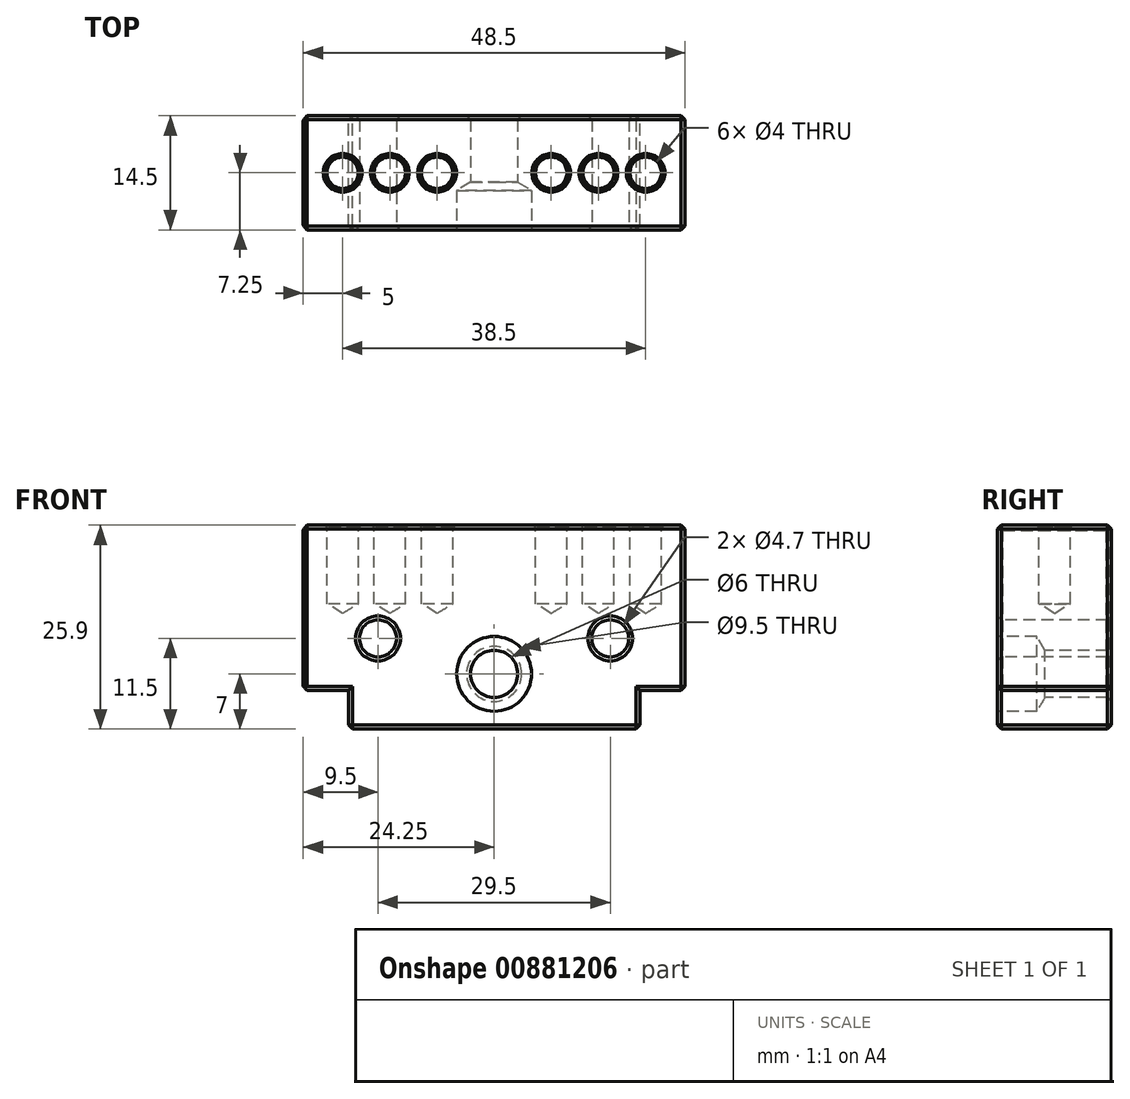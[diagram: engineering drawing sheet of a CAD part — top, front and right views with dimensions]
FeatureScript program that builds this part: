
annotation { "Feature Type Name" : "Feature", "Feature Type Description" : "" }
export const myFeature = defineFeature(function(context is Context, id is Id, definition is map)
    precondition{}
    {
        {
            var Q0;
            Q0=qCreatedBy(makeId("Front.planeOp"),FACE);
            var sketch = newSketch(context, id + "F0", { "sketchPlane" : qUnion([Q0])});
            skLineSegment(sketch, "E0", {"start": v(0, 4.9) * mm, "end": v(5.75, 4.9) * mm});
            skLineSegment(sketch, "E1", {"start": v(5.75, 4.9) * mm, "end": v(5.75, 0) * mm});
            skLineSegment(sketch, "E2", {"start": v(5.75, 0) * mm, "end": v(42.75, 0) * mm});
            skLineSegment(sketch, "E3", {"start": v(42.75, 0) * mm, "end": v(42.75, 4.9) * mm});
            skLineSegment(sketch, "E4", {"start": v(42.75, 4.9) * mm, "end": v(48.5, 4.9) * mm});
            skLineSegment(sketch, "E5", {"start": v(48.5, 4.9) * mm, "end": v(48.5, 25.9) * mm});
            skLineSegment(sketch, "E6", {"start": v(48.5, 25.9) * mm, "end": v(0, 25.9) * mm});
            skLineSegment(sketch, "E7", {"start": v(0, 25.9) * mm, "end": v(0, 4.9) * mm});
            skSolve(sketch);
        }
        {
            var Q0;
            Q0=makeQuery(id+"F0.imprint","IMPRINT",FACE,{"disambiguationData":[TD([[makeQuery(id+"F0.imprint","IMPRINT",EDGE,{"derivedFrom":sQuery(id+"F0.wireOp",EDGE,"E0")}),1.0]])]});
            extrude(context, id + "F1", {"entities" : qUnion([Q0]), "depth" : 14.5 * mm, "offsetDistance" : 25 * mm});
        }
        {
            var Q0;
            Q0=makeQuery(id+"F1.opExtrude","CAP_FACE",FACE,{"disambiguationData":[OSD([sQuery(id+"F0.wireOp",EDGE,"E0"),sQuery(id+"F0.wireOp",EDGE,"E1"),sQuery(id+"F0.wireOp",EDGE,"E2"),sQuery(id+"F0.wireOp",EDGE,"E3"),sQuery(id+"F0.wireOp",EDGE,"E4"),sQuery(id+"F0.wireOp",EDGE,"E5"),sQuery(id+"F0.wireOp",EDGE,"E6"),sQuery(id+"F0.wireOp",EDGE,"E7")])],"isStart":false});
            var sketch = newSketch(context, id + "F2", { "sketchPlane" : qUnion([Q0])});
            skPoint(sketch, "E8", {"position": v(24.25, 7) * mm});
            skPoint(sketch, "E9", {"position": v(9.5, 11.5) * mm});
            skPoint(sketch, "E10", {"position": v(39, 11.5) * mm});
            skPoint(sketch, "E11.end.orphan", {"position": v(0, 7) * mm});
            skSolve(sketch);
        }
        {
            var Q0;
            Q0=sQuery(id+"F2.wireOp",VERTEX,"E9");
            var Q1;
            Q1=sQuery(id+"F2.wireOp",VERTEX,"E10");
            var Q2;
            Q2=makeQuery(id+"F1.opExtrude","SWEPT_BODY",BODY,{"disambiguationData":[OSD([sQuery(id+"F0.wireOp",EDGE,"E0"),sQuery(id+"F0.wireOp",EDGE,"E1"),sQuery(id+"F0.wireOp",EDGE,"E2"),sQuery(id+"F0.wireOp",EDGE,"E3"),sQuery(id+"F0.wireOp",EDGE,"E4"),sQuery(id+"F0.wireOp",EDGE,"E5"),sQuery(id+"F0.wireOp",EDGE,"E6"),sQuery(id+"F0.wireOp",EDGE,"E7")])]});
            hole(context, id + "F3", {"style" : HoleStyle.SIMPLE, "endStyle" : HoleEndStyle.THROUGH, "holeDiameter" : 4.7 * mm, "majorDiameter" : 5 * mm, "isTappedThrough" : true, "tappedDepth" : 6 * mm, "tapClearance" : 3, "locations" : qUnion([Q0, Q1]), "scope" : qUnion([Q2])});
        }
        {
            var Q0;
            Q0=sQuery(id+"F2.wireOp",VERTEX,"E8");
            var Q1;
            Q1=makeQuery(id+"F1.opExtrude","SWEPT_BODY",BODY,{"disambiguationData":[OSD([sQuery(id+"F0.wireOp",EDGE,"E0"),sQuery(id+"F0.wireOp",EDGE,"E1"),sQuery(id+"F0.wireOp",EDGE,"E2"),sQuery(id+"F0.wireOp",EDGE,"E3"),sQuery(id+"F0.wireOp",EDGE,"E4"),sQuery(id+"F0.wireOp",EDGE,"E5"),sQuery(id+"F0.wireOp",EDGE,"E6"),sQuery(id+"F0.wireOp",EDGE,"E7")])]});
            hole(context, id + "F4", {"style" : HoleStyle.SIMPLE, "endStyle" : HoleEndStyle.THROUGH, "holeDiameter" : 6 * mm, "majorDiameter" : 5 * mm, "isTappedThrough" : true, "tappedDepth" : 6 * mm, "tapClearance" : 3, "locations" : qUnion([Q0]), "scope" : qUnion([Q1])});
        }
        {
            var Q0;
            Q0=makeQuery(id+"F1.opExtrude","SWEPT_FACE",FACE,{"disambiguationData":[OSD([sQuery(id+"F0.wireOp",EDGE,"E6")])]});
            var sketch = newSketch(context, id + "F5", { "sketchPlane" : qUnion([Q0])});
            skLineSegment(sketch, "E12", {"start": v(0, -7.25) * mm, "end": v(52.15, -7.25) * mm, "construction": true});
            skPoint(sketch, "E13", {"position": v(5, -7.25) * mm});
            skPoint(sketch, "E14", {"position": v(11, -7.25) * mm});
            skPoint(sketch, "E15", {"position": v(17, -7.25) * mm});
            skLineSegment(sketch, "E16", {"start": v(24.25, 0) * mm, "end": v(24.25, -16.26) * mm, "construction": true});
            skPoint(sketch, "E17.MirrorP", {"position": v(31.5, -7.25) * mm});
            skPoint(sketch, "E18.MirrorP", {"position": v(37.5, -7.25) * mm});
            skPoint(sketch, "E19.MirrorP", {"position": v(43.5, -7.25) * mm});
            skSolve(sketch);
        }
        {
            var Q0;
            Q0=sQuery(id+"F5.wireOp",VERTEX,"E13");
            var Q1;
            Q1=sQuery(id+"F5.wireOp",VERTEX,"E14");
            var Q2;
            Q2=sQuery(id+"F5.wireOp",VERTEX,"E15");
            var Q3;
            Q3=sQuery(id+"F5.wireOp",VERTEX,"E17.MirrorP");
            var Q4;
            Q4=sQuery(id+"F5.wireOp",VERTEX,"E18.MirrorP");
            var Q5;
            Q5=sQuery(id+"F5.wireOp",VERTEX,"E19.MirrorP");
            var Q6;
            Q6=makeQuery(id+"F1.opExtrude","SWEPT_BODY",BODY,{"disambiguationData":[OSD([sQuery(id+"F0.wireOp",EDGE,"E0"),sQuery(id+"F0.wireOp",EDGE,"E1"),sQuery(id+"F0.wireOp",EDGE,"E2"),sQuery(id+"F0.wireOp",EDGE,"E3"),sQuery(id+"F0.wireOp",EDGE,"E4"),sQuery(id+"F0.wireOp",EDGE,"E5"),sQuery(id+"F0.wireOp",EDGE,"E6"),sQuery(id+"F0.wireOp",EDGE,"E7")])]});
            hole(context, id + "F6", {"style" : HoleStyle.C_SINK, "endStyle" : HoleEndStyle.BLIND, "holeDiameter" : 4 * mm, "cSinkDiameter" : 4.5 * mm, "cSinkAngle" : 90 * degree, "majorDiameter" : 5 * mm, "holeDepth" : 10 * mm, "isTappedThrough" : true, "tappedDepth" : 6 * mm, "tapClearance" : 3, "locations" : qUnion([Q0, Q1, Q2, Q3, Q4, Q5]), "scope" : qUnion([Q6])});
        }
        {
            var Q0;
            Q0=makeQuery(id+"F1.opExtrude","SWEPT_FACE",FACE,{"disambiguationData":[OSD([sQuery(id+"F0.wireOp",EDGE,"E5")])]});
            var Q1;
            Q1=makeQuery(id+"F1.opExtrude","SWEPT_FACE",FACE,{"disambiguationData":[OSD([sQuery(id+"F0.wireOp",EDGE,"E6")])]});
            var Q2;
            Q2=makeQuery(id+"F1.opExtrude","CAP_FACE",FACE,{"disambiguationData":[OSD([sQuery(id+"F0.wireOp",EDGE,"E0"),sQuery(id+"F0.wireOp",EDGE,"E1"),sQuery(id+"F0.wireOp",EDGE,"E2"),sQuery(id+"F0.wireOp",EDGE,"E3"),sQuery(id+"F0.wireOp",EDGE,"E4"),sQuery(id+"F0.wireOp",EDGE,"E5"),sQuery(id+"F0.wireOp",EDGE,"E6"),sQuery(id+"F0.wireOp",EDGE,"E7")])],"isStart":false});
            var Q3;
            Q3=makeQuery(id+"F1.opExtrude","CAP_FACE",FACE,{"disambiguationData":[OSD([sQuery(id+"F0.wireOp",EDGE,"E0"),sQuery(id+"F0.wireOp",EDGE,"E1"),sQuery(id+"F0.wireOp",EDGE,"E2"),sQuery(id+"F0.wireOp",EDGE,"E3"),sQuery(id+"F0.wireOp",EDGE,"E4"),sQuery(id+"F0.wireOp",EDGE,"E5"),sQuery(id+"F0.wireOp",EDGE,"E6"),sQuery(id+"F0.wireOp",EDGE,"E7")])],"isStart":true});
            var Q4;
            Q4=makeQuery(id+"F1.opExtrude","SWEPT_FACE",FACE,{"disambiguationData":[OSD([sQuery(id+"F0.wireOp",EDGE,"E2")])]});
            chamfer(context, id + "F7", {"entities" : qUnion([Q0, Q1, Q2, Q3, Q4]), "width" : 0.5 * mm, "tangentPropagation" : true});
        }
        {
            var Q0;
            Q0=makeQuery(id+"F1.opExtrude","SWEPT_FACE",FACE,{"disambiguationData":[OSD([sQuery(id+"F0.wireOp",EDGE,"E7")])]});
            chamfer(context, id + "F8", {"entities" : qUnion([Q0]), "width" : 0.5 * mm, "tangentPropagation" : true});
        }
        {
            var Q0;
            Q0=sQuery(id+"F2.wireOp",VERTEX,"E8");
            var Q1;
            Q1=makeQuery(id+"F1.opExtrude","SWEPT_BODY",BODY,{"disambiguationData":[OSD([sQuery(id+"F0.wireOp",EDGE,"E0"),sQuery(id+"F0.wireOp",EDGE,"E1"),sQuery(id+"F0.wireOp",EDGE,"E2"),sQuery(id+"F0.wireOp",EDGE,"E3"),sQuery(id+"F0.wireOp",EDGE,"E4"),sQuery(id+"F0.wireOp",EDGE,"E5"),sQuery(id+"F0.wireOp",EDGE,"E6"),sQuery(id+"F0.wireOp",EDGE,"E7")])]});
            hole(context, id + "F9", {"style" : HoleStyle.SIMPLE, "endStyle" : HoleEndStyle.BLIND, "holeDiameter" : 9.5 * mm, "majorDiameter" : 5 * mm, "holeDepth" : 5 * mm, "isTappedThrough" : true, "tappedDepth" : 6 * mm, "tapClearance" : 3, "locations" : qUnion([Q0]), "scope" : qUnion([Q1])});
        }
    });
